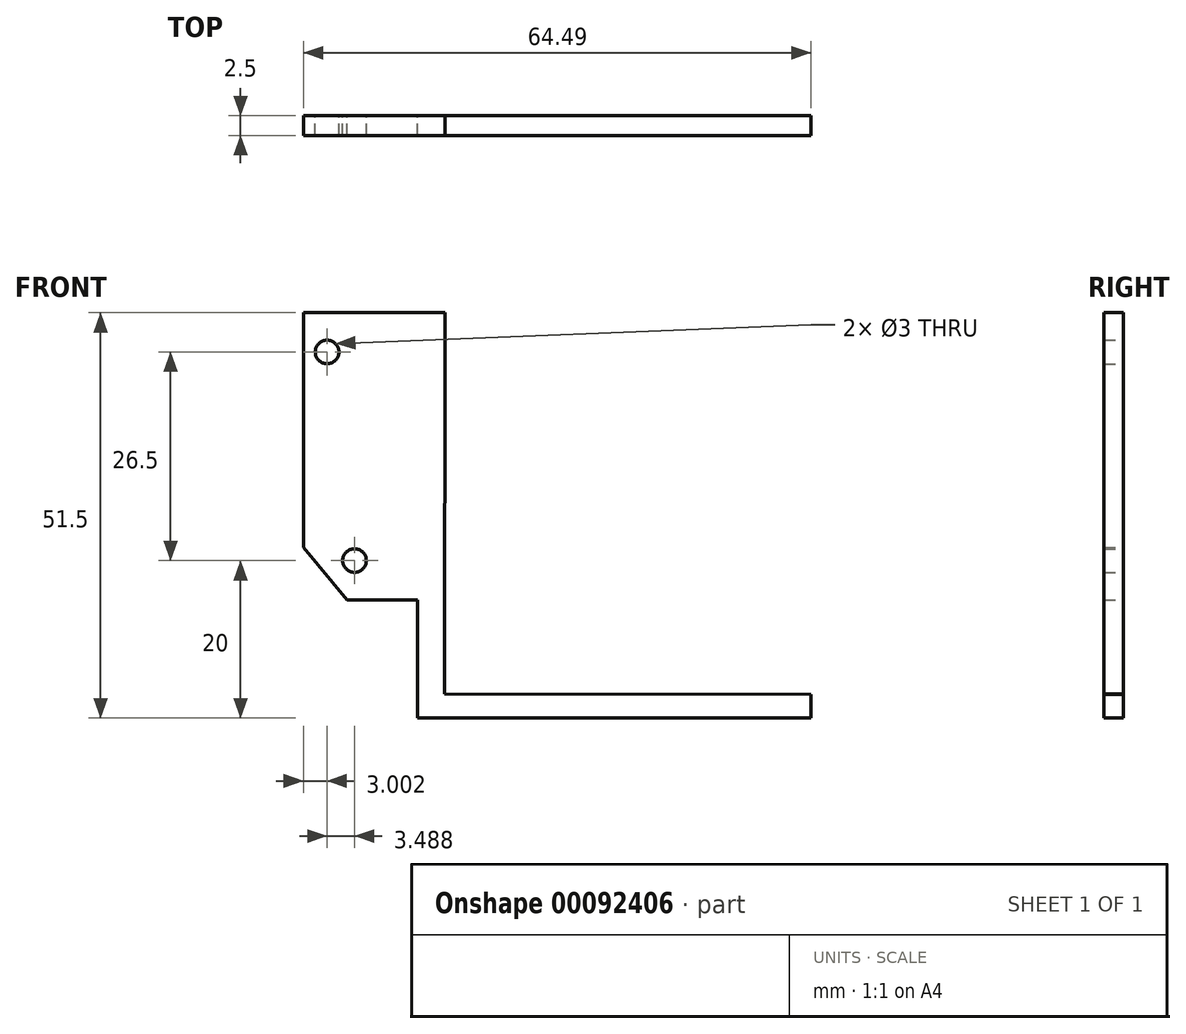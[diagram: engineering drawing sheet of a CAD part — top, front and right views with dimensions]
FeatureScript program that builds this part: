
annotation { "Feature Type Name" : "Feature", "Feature Type Description" : "" }
export const myFeature = defineFeature(function(context is Context, id is Id, definition is map)
    precondition{}
    {
        {
            var Q0;
            Q0=qCreatedBy(makeId("Front.planeOp"),FACE);
            var sketch = newSketch(context, id + "F0", { "sketchPlane" : qUnion([Q0])});
            skLineSegment(sketch, "E0", {"start": v(50, 0) * mm, "end": v(0, 0) * mm});
            skLineSegment(sketch, "E1", {"start": v(-8.95, 15) * mm, "end": v(0, 15) * mm});
            skCircle(sketch, "E2", {"center": v(-11.49, 46.5) * mm, "radius": 1.5 * mm});
            skCircle(sketch, "E3", {"center": v(-8, 20) * mm, "radius": 1.5 * mm});
            skLineSegment(sketch, "E4", {"start": v(-14.49, 51.5) * mm, "end": v(3.51, 51.5) * mm});
            skLineSegment(sketch, "E5", {"start": v(3.42, 3.09) * mm, "end": v(3.51, 51.5) * mm});
            skLineSegment(sketch, "E6", {"start": v(0, 0) * mm, "end": v(0, 15) * mm});
            skLineSegment(sketch, "E7", {"start": v(-14.49, 51.5) * mm, "end": v(-14.49, 21.66) * mm});
            skLineSegment(sketch, "E8", {"start": v(3.42, 3.09) * mm, "end": v(50, 3) * mm});
            skLineSegment(sketch, "E9", {"start": v(50, 3) * mm, "end": v(50, 0) * mm});
            skLineSegment(sketch, "E10", {"start": v(-14.49, 21.66) * mm, "end": v(-8.95, 15) * mm});
            skSolve(sketch);
        }
        {
            var Q0;
            Q0=makeQuery(id+"F0.imprint","IMPRINT",FACE,{"disambiguationData":[TD([[makeQuery(id+"F0.imprint","IMPRINT",EDGE,{"derivedFrom":sQuery(id+"F0.wireOp",EDGE,"E0")}),-1.0]])]});
            extrude(context, id + "F1", {"entities" : qUnion([Q0]), "endBound" : BoundingType.SYMMETRIC, "depth" : 2.5 * mm});
        }
    });
